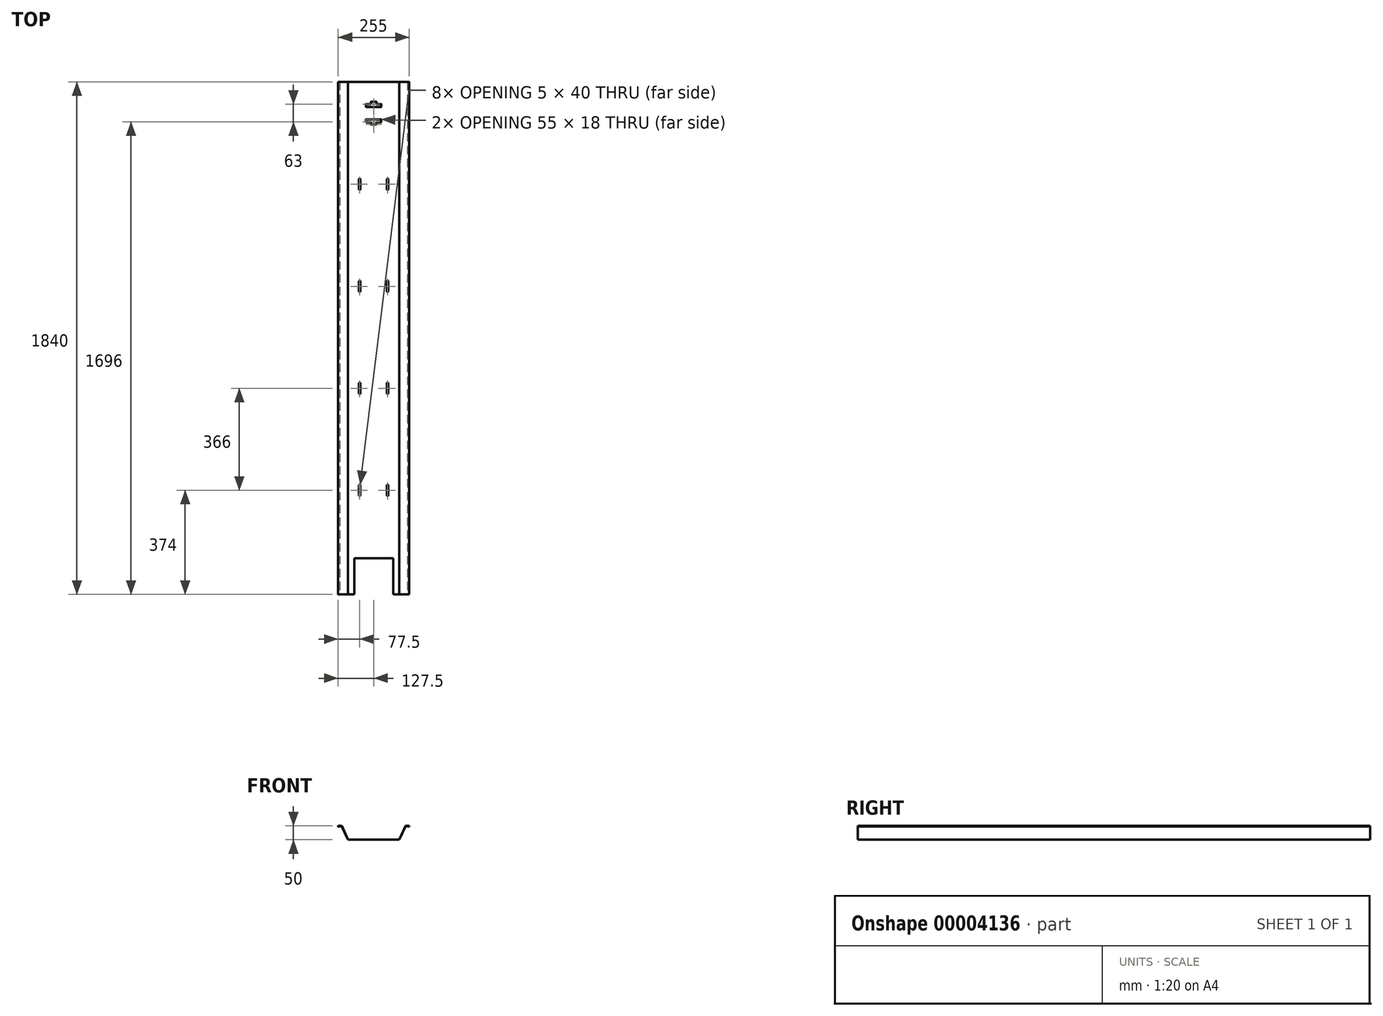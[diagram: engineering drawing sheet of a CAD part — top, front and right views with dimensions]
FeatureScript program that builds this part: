
annotation { "Feature Type Name" : "Feature", "Feature Type Description" : "" }
export const myFeature = defineFeature(function(context is Context, id is Id, definition is map)
    precondition{}
    {
        {
            var Q0;
            Q0=qCreatedBy(makeId("Front.planeOp"),FACE);
            var sketch = newSketch(context, id + "F0", { "sketchPlane" : qUnion([Q0])});
            skLineSegment(sketch, "E0", {"start": v(-92.5, 0) * mm, "end": v(0, 0) * mm});
            skLineSegment(sketch, "E1.0", {"start": v(-126.5, 48) * mm, "end": v(-121.5, 48) * mm});
            skLineSegment(sketch, "E1.1", {"start": v(-126.5, 49) * mm, "end": v(-126.5, 48) * mm});
            skLineSegment(sketch, "E1.2", {"start": v(-115.14, 49) * mm, "end": v(-126.5, 49) * mm});
            skLineSegment(sketch, "E2", {"start": v(-92.5, 0) * mm, "end": v(-115.14, 49) * mm});
            skLineSegment(sketch, "E3.0", {"start": v(-127.5, 47) * mm, "end": v(-121.5, 47) * mm});
            skLineSegment(sketch, "E3.1", {"start": v(-127.5, 50) * mm, "end": v(-127.5, 47) * mm});
            skLineSegment(sketch, "E3.2", {"start": v(-114.5, 50) * mm, "end": v(-127.5, 50) * mm});
            skLineSegment(sketch, "E3.3", {"start": v(-91.86, 1) * mm, "end": v(-114.5, 50) * mm});
            skLineSegment(sketch, "E3.4", {"start": v(-91.86, 1) * mm, "end": v(0, 1) * mm});
            skLineSegment(sketch, "E4", {"start": v(-121.5, 48) * mm, "end": v(-121.5, 47) * mm});
            skLineSegment(sketch, "E5.0.MirrorCS", {"start": v(91.86, 1) * mm, "end": v(0, 1) * mm});
            skLineSegment(sketch, "E5.1.MirrorCS", {"start": v(92.5, 0) * mm, "end": v(0, 0) * mm});
            skLineSegment(sketch, "E5.2.MirrorCS", {"start": v(92.5, 0) * mm, "end": v(115.14, 49) * mm});
            skLineSegment(sketch, "E5.3.MirrorCS", {"start": v(91.86, 1) * mm, "end": v(114.5, 50) * mm});
            skLineSegment(sketch, "E5.4.MirrorCS", {"start": v(114.5, 50) * mm, "end": v(127.5, 50) * mm});
            skLineSegment(sketch, "E5.5.MirrorCS", {"start": v(115.14, 49) * mm, "end": v(126.5, 49) * mm});
            skLineSegment(sketch, "E5.6.MirrorCS", {"start": v(126.5, 49) * mm, "end": v(126.5, 48) * mm});
            skLineSegment(sketch, "E5.7.MirrorCS", {"start": v(126.5, 48) * mm, "end": v(121.5, 48) * mm});
            skLineSegment(sketch, "E5.8.MirrorCS", {"start": v(121.5, 48) * mm, "end": v(121.5, 47) * mm});
            skLineSegment(sketch, "E5.9.MirrorCS", {"start": v(127.5, 50) * mm, "end": v(127.5, 47) * mm});
            skLineSegment(sketch, "E5.10.MirrorCS", {"start": v(127.5, 47) * mm, "end": v(121.5, 47) * mm});
            skSolve(sketch);
        }
        {
            var Q0;
            Q0=makeQuery(id+"F0.imprint","IMPRINT",FACE,{"disambiguationData":[TD([[makeQuery(id+"F0.imprint","IMPRINT",EDGE,{"derivedFrom":sQuery(id+"F0.wireOp",EDGE,"E0")}),1.0]])]});
            extrude(context, id + "F1", {"entities" : qUnion([Q0]), "oppositeDirection" : true, "depth" : 1840 * mm});
        }
        {
            var Q0;
            Q0=makeQuery(id+"F1.opExtrude","SWEPT_EDGE",EDGE,{"disambiguationData":[OSD([sQuery(id+"F0.wireOp",EDGE,"E3.0"),sQuery(id+"F0.wireOp",EDGE,"E3.1")])]});
            var Q1;
            Q1=makeQuery(id+"F1.opExtrude","SWEPT_EDGE",EDGE,{"disambiguationData":[OSD([sQuery(id+"F0.wireOp",EDGE,"E3.1"),sQuery(id+"F0.wireOp",EDGE,"E3.2")])]});
            var Q2;
            Q2=makeQuery(id+"F1.opExtrude","SWEPT_EDGE",EDGE,{"disambiguationData":[OSD([sQuery(id+"F0.wireOp",EDGE,"E3.2"),sQuery(id+"F0.wireOp",EDGE,"E3.3")])]});
            var Q3;
            Q3=makeQuery(id+"F1.opExtrude","SWEPT_EDGE",EDGE,{"disambiguationData":[OSD([sQuery(id+"F0.wireOp",EDGE,"E5.4.MirrorCS"),sQuery(id+"F0.wireOp",EDGE,"E5.9.MirrorCS")])]});
            var Q4;
            Q4=makeQuery(id+"F1.opExtrude","SWEPT_EDGE",EDGE,{"disambiguationData":[OSD([sQuery(id+"F0.wireOp",EDGE,"E5.9.MirrorCS"),sQuery(id+"F0.wireOp",EDGE,"E5.10.MirrorCS")])]});
            var Q5;
            Q5=makeQuery(id+"F1.opExtrude","SWEPT_EDGE",EDGE,{"disambiguationData":[OSD([sQuery(id+"F0.wireOp",EDGE,"E5.3.MirrorCS"),sQuery(id+"F0.wireOp",EDGE,"E5.4.MirrorCS")])]});
            fillet(context, id + "F2", {"entities" : qUnion([Q0, Q1, Q2, Q3, Q4, Q5]), "radius" : 0.2 * mm, "tangentPropagation" : true, "allowEdgeOverflow" : false});
        }
        {
            var Q0;
            Q0=makeQuery(id+"F1.opExtrude","SWEPT_EDGE",EDGE,{"disambiguationData":[OSD([sQuery(id+"F0.wireOp",EDGE,"E5.7.MirrorCS"),sQuery(id+"F0.wireOp",EDGE,"E5.8.MirrorCS")])]});
            var Q1;
            Q1=makeQuery(id+"F1.opExtrude","SWEPT_EDGE",EDGE,{"disambiguationData":[OSD([sQuery(id+"F0.wireOp",EDGE,"E5.8.MirrorCS"),sQuery(id+"F0.wireOp",EDGE,"E5.10.MirrorCS")])]});
            var Q2;
            Q2=makeQuery(id+"F1.opExtrude","SWEPT_EDGE",EDGE,{"disambiguationData":[OSD([sQuery(id+"F0.wireOp",EDGE,"E5.5.MirrorCS"),sQuery(id+"F0.wireOp",EDGE,"E5.6.MirrorCS")])]});
            var Q3;
            Q3=makeQuery(id+"F1.opExtrude","SWEPT_EDGE",EDGE,{"disambiguationData":[OSD([sQuery(id+"F0.wireOp",EDGE,"E5.2.MirrorCS"),sQuery(id+"F0.wireOp",EDGE,"E5.5.MirrorCS")])]});
            var Q4;
            Q4=makeQuery(id+"F1.opExtrude","SWEPT_EDGE",EDGE,{"disambiguationData":[OSD([sQuery(id+"F0.wireOp",EDGE,"E5.6.MirrorCS"),sQuery(id+"F0.wireOp",EDGE,"E5.7.MirrorCS")])]});
            var Q5;
            Q5=makeQuery(id+"F1.opExtrude","SWEPT_EDGE",EDGE,{"disambiguationData":[OSD([sQuery(id+"F0.wireOp",EDGE,"E1.0"),sQuery(id+"F0.wireOp",EDGE,"E1.1")])]});
            var Q6;
            Q6=makeQuery(id+"F1.opExtrude","SWEPT_EDGE",EDGE,{"disambiguationData":[OSD([sQuery(id+"F0.wireOp",EDGE,"E1.0"),sQuery(id+"F0.wireOp",EDGE,"E4")])]});
            var Q7;
            Q7=makeQuery(id+"F1.opExtrude","SWEPT_EDGE",EDGE,{"disambiguationData":[OSD([sQuery(id+"F0.wireOp",EDGE,"E3.0"),sQuery(id+"F0.wireOp",EDGE,"E4")])]});
            var Q8;
            Q8=makeQuery(id+"F1.opExtrude","SWEPT_EDGE",EDGE,{"disambiguationData":[OSD([sQuery(id+"F0.wireOp",EDGE,"E1.1"),sQuery(id+"F0.wireOp",EDGE,"E1.2")])]});
            var Q9;
            Q9=makeQuery(id+"F1.opExtrude","SWEPT_EDGE",EDGE,{"disambiguationData":[OSD([sQuery(id+"F0.wireOp",EDGE,"E1.2"),sQuery(id+"F0.wireOp",EDGE,"E2")])]});
            fillet(context, id + "F3", {"entities" : qUnion([Q0, Q1, Q2, Q3, Q4, Q5, Q6, Q7, Q8, Q9]), "radius" : 0.1 * mm, "tangentPropagation" : true, "allowEdgeOverflow" : false});
        }
        {
            var Q0;
            Q0=makeQuery(id+"F1.opExtrude","SWEPT_FACE",FACE,{"disambiguationData":[OSD([sQuery(id+"F0.wireOp",EDGE,"E5.0.MirrorCS")])]});
            var sketch = newSketch(context, id + "F4", { "sketchPlane" : qUnion([Q0])});
            skLineSegment(sketch, "E6", {"start": v(0, 0) * mm, "end": v(-70, 0) * mm});
            skLineSegment(sketch, "E7", {"start": v(-70, 0) * mm, "end": v(-70, 130) * mm});
            skLineSegment(sketch, "E8", {"start": v(-70, 130) * mm, "end": v(70, 130) * mm});
            skLineSegment(sketch, "E9", {"start": v(70, 130) * mm, "end": v(70, 0) * mm});
            skLineSegment(sketch, "E10", {"start": v(70, 0) * mm, "end": v(0, 0) * mm});
            skLineSegment(sketch, "E11", {"start": v(0, 1840) * mm, "end": v(0, 0) * mm, "construction": true});
            skLineSegment(sketch, "E12", {"start": v(0, 1750) * mm, "end": v(-27.5, 1750) * mm});
            skLineSegment(sketch, "E13", {"start": v(-27.5, 1750) * mm, "end": v(-27.5, 1760) * mm});
            skLineSegment(sketch, "E14", {"start": v(-27.5, 1760) * mm, "end": v(-10, 1760) * mm});
            skLineSegment(sketch, "E15", {"start": v(-10, 1760) * mm, "end": v(-10, 1768) * mm});
            skLineSegment(sketch, "E16", {"start": v(-10, 1768) * mm, "end": v(0, 1768) * mm});
            skLineSegment(sketch, "E17", {"start": v(0, 1768) * mm, "end": v(10, 1768) * mm});
            skLineSegment(sketch, "E18", {"start": v(10, 1768) * mm, "end": v(10, 1760) * mm});
            skLineSegment(sketch, "E19", {"start": v(10, 1760) * mm, "end": v(27.5, 1760) * mm});
            skLineSegment(sketch, "E20", {"start": v(27.5, 1760) * mm, "end": v(27.5, 1750) * mm});
            skLineSegment(sketch, "E21", {"start": v(27.5, 1750) * mm, "end": v(0, 1750) * mm});
            skLineSegment(sketch, "E22", {"start": v(0, 1705) * mm, "end": v(27.5, 1705) * mm});
            skLineSegment(sketch, "E23", {"start": v(27.5, 1705) * mm, "end": v(27.5, 1695) * mm});
            skLineSegment(sketch, "E24", {"start": v(27.5, 1695) * mm, "end": v(10, 1695) * mm});
            skLineSegment(sketch, "E25", {"start": v(10, 1695) * mm, "end": v(10, 1687) * mm});
            skLineSegment(sketch, "E26", {"start": v(10, 1687) * mm, "end": v(-10, 1687) * mm});
            skLineSegment(sketch, "E27", {"start": v(-10, 1687) * mm, "end": v(-10, 1695) * mm});
            skLineSegment(sketch, "E28", {"start": v(-10, 1695) * mm, "end": v(-27.5, 1695) * mm});
            skLineSegment(sketch, "E29", {"start": v(-27.5, 1695) * mm, "end": v(-27.5, 1705) * mm});
            skLineSegment(sketch, "E30", {"start": v(-27.5, 1705) * mm, "end": v(0, 1705) * mm});
            skLineSegment(sketch, "E31", {"start": v(-91.86, 1472) * mm, "end": v(91.86, 1472) * mm, "construction": true});
            skLineSegment(sketch, "E32", {"start": v(-91.86, 1106) * mm, "end": v(91.86, 1106) * mm, "construction": true});
            skLineSegment(sketch, "E33", {"start": v(-91.86, 740) * mm, "end": v(91.86, 740) * mm, "construction": true});
            skLineSegment(sketch, "E34", {"start": v(-91.86, 374) * mm, "end": v(91.86, 374) * mm, "construction": true});
            skLineSegment(sketch, "E35", {"start": v(50, 1840) * mm, "end": v(50, 0) * mm, "construction": true});
            skLineSegment(sketch, "E36", {"start": v(-50, 1840) * mm, "end": v(-50, 0) * mm, "construction": true});
            skLineSegment(sketch, "E37.rect.bottom", {"start": v(52.5, 354) * mm, "end": v(47.5, 354) * mm});
            skLineSegment(sketch, "E37.rect.top", {"start": v(52.5, 394) * mm, "end": v(47.5, 394) * mm});
            skLineSegment(sketch, "E37.rect.left", {"start": v(52.5, 354) * mm, "end": v(52.5, 394) * mm});
            skLineSegment(sketch, "E37.rect.right", {"start": v(47.5, 354) * mm, "end": v(47.5, 394) * mm});
            skPoint(sketch, "E37.rect.middle", {"position": v(50, 374) * mm});
            skLineSegment(sketch, "E38.rect.bottom", {"start": v(-47.5, 354) * mm, "end": v(-52.5, 354) * mm});
            skLineSegment(sketch, "E38.rect.top", {"start": v(-47.5, 394) * mm, "end": v(-52.5, 394) * mm});
            skLineSegment(sketch, "E38.rect.left", {"start": v(-47.5, 354) * mm, "end": v(-47.5, 394) * mm});
            skLineSegment(sketch, "E38.rect.right", {"start": v(-52.5, 354) * mm, "end": v(-52.5, 394) * mm});
            skPoint(sketch, "E38.rect.middle", {"position": v(-50, 374) * mm});
            skLineSegment(sketch, "E39.rect.bottom", {"start": v(-47.5, 720) * mm, "end": v(-52.5, 720) * mm});
            skLineSegment(sketch, "E39.rect.top", {"start": v(-47.5, 760) * mm, "end": v(-52.5, 760) * mm});
            skLineSegment(sketch, "E39.rect.left", {"start": v(-47.5, 720) * mm, "end": v(-47.5, 760) * mm});
            skLineSegment(sketch, "E39.rect.right", {"start": v(-52.5, 720) * mm, "end": v(-52.5, 760) * mm});
            skPoint(sketch, "E39.rect.middle", {"position": v(-50, 740) * mm});
            skLineSegment(sketch, "E40.rect.bottom", {"start": v(52.5, 720) * mm, "end": v(47.5, 720) * mm});
            skLineSegment(sketch, "E40.rect.top", {"start": v(52.5, 760) * mm, "end": v(47.5, 760) * mm});
            skLineSegment(sketch, "E40.rect.left", {"start": v(52.5, 720) * mm, "end": v(52.5, 760) * mm});
            skLineSegment(sketch, "E40.rect.right", {"start": v(47.5, 720) * mm, "end": v(47.5, 760) * mm});
            skPoint(sketch, "E40.rect.middle", {"position": v(50, 740) * mm});
            skLineSegment(sketch, "E41.rect.bottom", {"start": v(-47.5, 1086) * mm, "end": v(-52.5, 1086) * mm});
            skLineSegment(sketch, "E41.rect.top", {"start": v(-47.5, 1126) * mm, "end": v(-52.5, 1126) * mm});
            skLineSegment(sketch, "E41.rect.left", {"start": v(-47.5, 1086) * mm, "end": v(-47.5, 1126) * mm});
            skLineSegment(sketch, "E41.rect.right", {"start": v(-52.5, 1086) * mm, "end": v(-52.5, 1126) * mm});
            skPoint(sketch, "E41.rect.middle", {"position": v(-50, 1106) * mm});
            skLineSegment(sketch, "E42.rect.bottom", {"start": v(52.5, 1086) * mm, "end": v(47.5, 1086) * mm});
            skLineSegment(sketch, "E42.rect.top", {"start": v(52.5, 1126) * mm, "end": v(47.5, 1126) * mm});
            skLineSegment(sketch, "E42.rect.left", {"start": v(52.5, 1086) * mm, "end": v(52.5, 1126) * mm});
            skLineSegment(sketch, "E42.rect.right", {"start": v(47.5, 1086) * mm, "end": v(47.5, 1126) * mm});
            skPoint(sketch, "E42.rect.middle", {"position": v(50, 1106) * mm});
            skLineSegment(sketch, "E43.rect.bottom", {"start": v(-47.5, 1452) * mm, "end": v(-52.5, 1452) * mm});
            skLineSegment(sketch, "E43.rect.top", {"start": v(-47.5, 1492) * mm, "end": v(-52.5, 1492) * mm});
            skLineSegment(sketch, "E43.rect.left", {"start": v(-47.5, 1452) * mm, "end": v(-47.5, 1492) * mm});
            skLineSegment(sketch, "E43.rect.right", {"start": v(-52.5, 1452) * mm, "end": v(-52.5, 1492) * mm});
            skPoint(sketch, "E43.rect.middle", {"position": v(-50, 1472) * mm});
            skLineSegment(sketch, "E44.rect.bottom", {"start": v(52.5, 1452) * mm, "end": v(47.5, 1452) * mm});
            skLineSegment(sketch, "E44.rect.top", {"start": v(52.5, 1492) * mm, "end": v(47.5, 1492) * mm});
            skLineSegment(sketch, "E44.rect.left", {"start": v(52.5, 1452) * mm, "end": v(52.5, 1492) * mm});
            skLineSegment(sketch, "E44.rect.right", {"start": v(47.5, 1452) * mm, "end": v(47.5, 1492) * mm});
            skPoint(sketch, "E44.rect.middle", {"position": v(50, 1472) * mm});
            skSolve(sketch);
        }
        {
            var Q0;
            Q0=makeQuery(id+"F4.imprint","IMPRINT",FACE,{"disambiguationData":[TD([[makeQuery(id+"F4.imprint","IMPRINT",EDGE,{"derivedFrom":sQuery(id+"F4.wireOp",EDGE,"E6")}),-1.0]])]});
            var Q1;
            Q1=makeQuery(id+"F4.imprint","IMPRINT",FACE,{"disambiguationData":[TD([[makeQuery(id+"F4.imprint","IMPRINT",EDGE,{"derivedFrom":sQuery(id+"F4.wireOp",EDGE,"E37.rect.bottom")}),-1.0]])]});
            var Q2;
            Q2=makeQuery(id+"F4.imprint","IMPRINT",FACE,{"disambiguationData":[TD([[makeQuery(id+"F4.imprint","IMPRINT",EDGE,{"derivedFrom":sQuery(id+"F4.wireOp",EDGE,"E38.rect.bottom")}),-1.0]])]});
            var Q3;
            Q3=makeQuery(id+"F4.imprint","IMPRINT",FACE,{"disambiguationData":[TD([[makeQuery(id+"F4.imprint","IMPRINT",EDGE,{"derivedFrom":sQuery(id+"F4.wireOp",EDGE,"E39.rect.bottom")}),-1.0]])]});
            var Q4;
            Q4=makeQuery(id+"F4.imprint","IMPRINT",FACE,{"disambiguationData":[TD([[makeQuery(id+"F4.imprint","IMPRINT",EDGE,{"derivedFrom":sQuery(id+"F4.wireOp",EDGE,"E40.rect.bottom")}),-1.0]])]});
            var Q5;
            Q5=makeQuery(id+"F4.imprint","IMPRINT",FACE,{"disambiguationData":[TD([[makeQuery(id+"F4.imprint","IMPRINT",EDGE,{"derivedFrom":sQuery(id+"F4.wireOp",EDGE,"E42.rect.bottom")}),-1.0]])]});
            var Q6;
            Q6=makeQuery(id+"F4.imprint","IMPRINT",FACE,{"disambiguationData":[TD([[makeQuery(id+"F4.imprint","IMPRINT",EDGE,{"derivedFrom":sQuery(id+"F4.wireOp",EDGE,"E41.rect.bottom")}),-1.0]])]});
            var Q7;
            Q7=makeQuery(id+"F4.imprint","IMPRINT",FACE,{"disambiguationData":[TD([[makeQuery(id+"F4.imprint","IMPRINT",EDGE,{"derivedFrom":sQuery(id+"F4.wireOp",EDGE,"E44.rect.bottom")}),-1.0]])]});
            var Q8;
            Q8=makeQuery(id+"F4.imprint","IMPRINT",FACE,{"disambiguationData":[TD([[makeQuery(id+"F4.imprint","IMPRINT",EDGE,{"derivedFrom":sQuery(id+"F4.wireOp",EDGE,"E43.rect.bottom")}),-1.0]])]});
            var Q9;
            Q9=makeQuery(id+"F4.imprint","IMPRINT",FACE,{"disambiguationData":[TD([[makeQuery(id+"F4.imprint","IMPRINT",EDGE,{"derivedFrom":sQuery(id+"F4.wireOp",EDGE,"E22")}),-1.0]])]});
            var Q10;
            Q10=makeQuery(id+"F4.imprint","IMPRINT",FACE,{"disambiguationData":[TD([[makeQuery(id+"F4.imprint","IMPRINT",EDGE,{"derivedFrom":sQuery(id+"F4.wireOp",EDGE,"E12")}),-1.0]])]});
            extrude(context, id + "F5", {"entities" : qUnion([Q0, Q1, Q2, Q3, Q4, Q5, Q6, Q7, Q8, Q9, Q10]), "operationType" : NewBodyOperationType.REMOVE, "oppositeDirection" : true, "depth" : 25 * mm});
        }
        {
            var Q0;
            Q0=makeQuery(id+"F5.boolean.opBoolean","COPY",EDGE,{"derivedFrom":makeQuery(id+"F5.opExtrude","SWEPT_EDGE",EDGE,{"disambiguationData":[OSD([sQuery(id+"F4.wireOp",EDGE,"E38.rect.top"),sQuery(id+"F4.wireOp",EDGE,"E38.rect.right")])]})});
            var Q1;
            Q1=makeQuery(id+"F5.boolean.opBoolean","COPY",EDGE,{"derivedFrom":makeQuery(id+"F5.opExtrude","SWEPT_EDGE",EDGE,{"disambiguationData":[OSD([sQuery(id+"F4.wireOp",EDGE,"E38.rect.top"),sQuery(id+"F4.wireOp",EDGE,"E38.rect.left")])]})});
            var Q2;
            Q2=makeQuery(id+"F5.boolean.opBoolean","COPY",EDGE,{"derivedFrom":makeQuery(id+"F5.opExtrude","SWEPT_EDGE",EDGE,{"disambiguationData":[OSD([sQuery(id+"F4.wireOp",EDGE,"E38.rect.bottom"),sQuery(id+"F4.wireOp",EDGE,"E38.rect.right")])]})});
            var Q3;
            Q3=makeQuery(id+"F5.boolean.opBoolean","COPY",EDGE,{"derivedFrom":makeQuery(id+"F5.opExtrude","SWEPT_EDGE",EDGE,{"disambiguationData":[OSD([sQuery(id+"F4.wireOp",EDGE,"E38.rect.bottom"),sQuery(id+"F4.wireOp",EDGE,"E38.rect.left")])]})});
            var Q4;
            Q4=makeQuery(id+"F5.boolean.opBoolean","COPY",EDGE,{"derivedFrom":makeQuery(id+"F5.opExtrude","SWEPT_EDGE",EDGE,{"disambiguationData":[OSD([sQuery(id+"F4.wireOp",EDGE,"E37.rect.bottom"),sQuery(id+"F4.wireOp",EDGE,"E37.rect.right")])]})});
            var Q5;
            Q5=makeQuery(id+"F5.boolean.opBoolean","COPY",EDGE,{"derivedFrom":makeQuery(id+"F5.opExtrude","SWEPT_EDGE",EDGE,{"disambiguationData":[OSD([sQuery(id+"F4.wireOp",EDGE,"E37.rect.bottom"),sQuery(id+"F4.wireOp",EDGE,"E37.rect.left")])]})});
            var Q6;
            Q6=makeQuery(id+"F5.boolean.opBoolean","COPY",EDGE,{"derivedFrom":makeQuery(id+"F5.opExtrude","SWEPT_EDGE",EDGE,{"disambiguationData":[OSD([sQuery(id+"F4.wireOp",EDGE,"E37.rect.top"),sQuery(id+"F4.wireOp",EDGE,"E37.rect.left")])]})});
            var Q7;
            Q7=makeQuery(id+"F5.boolean.opBoolean","COPY",EDGE,{"derivedFrom":makeQuery(id+"F5.opExtrude","SWEPT_EDGE",EDGE,{"disambiguationData":[OSD([sQuery(id+"F4.wireOp",EDGE,"E37.rect.top"),sQuery(id+"F4.wireOp",EDGE,"E37.rect.right")])]})});
            var Q8;
            Q8=makeQuery(id+"F5.boolean.opBoolean","COPY",EDGE,{"derivedFrom":makeQuery(id+"F5.opExtrude","SWEPT_EDGE",EDGE,{"disambiguationData":[OSD([sQuery(id+"F4.wireOp",EDGE,"E39.rect.top"),sQuery(id+"F4.wireOp",EDGE,"E39.rect.right")])]})});
            var Q9;
            Q9=makeQuery(id+"F5.boolean.opBoolean","COPY",EDGE,{"derivedFrom":makeQuery(id+"F5.opExtrude","SWEPT_EDGE",EDGE,{"disambiguationData":[OSD([sQuery(id+"F4.wireOp",EDGE,"E39.rect.top"),sQuery(id+"F4.wireOp",EDGE,"E39.rect.left")])]})});
            var Q10;
            Q10=makeQuery(id+"F5.boolean.opBoolean","COPY",EDGE,{"derivedFrom":makeQuery(id+"F5.opExtrude","SWEPT_EDGE",EDGE,{"disambiguationData":[OSD([sQuery(id+"F4.wireOp",EDGE,"E39.rect.bottom"),sQuery(id+"F4.wireOp",EDGE,"E39.rect.right")])]})});
            var Q11;
            Q11=makeQuery(id+"F5.boolean.opBoolean","COPY",EDGE,{"derivedFrom":makeQuery(id+"F5.opExtrude","SWEPT_EDGE",EDGE,{"disambiguationData":[OSD([sQuery(id+"F4.wireOp",EDGE,"E39.rect.bottom"),sQuery(id+"F4.wireOp",EDGE,"E39.rect.left")])]})});
            var Q12;
            Q12=makeQuery(id+"F5.boolean.opBoolean","COPY",EDGE,{"derivedFrom":makeQuery(id+"F5.opExtrude","SWEPT_EDGE",EDGE,{"disambiguationData":[OSD([sQuery(id+"F4.wireOp",EDGE,"E40.rect.bottom"),sQuery(id+"F4.wireOp",EDGE,"E40.rect.left")])]})});
            var Q13;
            Q13=makeQuery(id+"F5.boolean.opBoolean","COPY",EDGE,{"derivedFrom":makeQuery(id+"F5.opExtrude","SWEPT_EDGE",EDGE,{"disambiguationData":[OSD([sQuery(id+"F4.wireOp",EDGE,"E40.rect.bottom"),sQuery(id+"F4.wireOp",EDGE,"E40.rect.right")])]})});
            var Q14;
            Q14=makeQuery(id+"F5.boolean.opBoolean","COPY",EDGE,{"derivedFrom":makeQuery(id+"F5.opExtrude","SWEPT_EDGE",EDGE,{"disambiguationData":[OSD([sQuery(id+"F4.wireOp",EDGE,"E40.rect.top"),sQuery(id+"F4.wireOp",EDGE,"E40.rect.right")])]})});
            var Q15;
            Q15=makeQuery(id+"F5.boolean.opBoolean","COPY",EDGE,{"derivedFrom":makeQuery(id+"F5.opExtrude","SWEPT_EDGE",EDGE,{"disambiguationData":[OSD([sQuery(id+"F4.wireOp",EDGE,"E40.rect.top"),sQuery(id+"F4.wireOp",EDGE,"E40.rect.left")])]})});
            var Q16;
            Q16=makeQuery(id+"F5.boolean.opBoolean","COPY",EDGE,{"derivedFrom":makeQuery(id+"F5.opExtrude","SWEPT_EDGE",EDGE,{"disambiguationData":[OSD([sQuery(id+"F4.wireOp",EDGE,"E42.rect.top"),sQuery(id+"F4.wireOp",EDGE,"E42.rect.left")])]})});
            var Q17;
            Q17=makeQuery(id+"F5.boolean.opBoolean","COPY",EDGE,{"derivedFrom":makeQuery(id+"F5.opExtrude","SWEPT_EDGE",EDGE,{"disambiguationData":[OSD([sQuery(id+"F4.wireOp",EDGE,"E42.rect.top"),sQuery(id+"F4.wireOp",EDGE,"E42.rect.right")])]})});
            var Q18;
            Q18=makeQuery(id+"F5.boolean.opBoolean","COPY",EDGE,{"derivedFrom":makeQuery(id+"F5.opExtrude","SWEPT_EDGE",EDGE,{"disambiguationData":[OSD([sQuery(id+"F4.wireOp",EDGE,"E42.rect.bottom"),sQuery(id+"F4.wireOp",EDGE,"E42.rect.left")])]})});
            var Q19;
            Q19=makeQuery(id+"F5.boolean.opBoolean","COPY",EDGE,{"derivedFrom":makeQuery(id+"F5.opExtrude","SWEPT_EDGE",EDGE,{"disambiguationData":[OSD([sQuery(id+"F4.wireOp",EDGE,"E42.rect.bottom"),sQuery(id+"F4.wireOp",EDGE,"E42.rect.right")])]})});
            var Q20;
            Q20=makeQuery(id+"F5.boolean.opBoolean","COPY",EDGE,{"derivedFrom":makeQuery(id+"F5.opExtrude","SWEPT_EDGE",EDGE,{"disambiguationData":[OSD([sQuery(id+"F4.wireOp",EDGE,"E41.rect.bottom"),sQuery(id+"F4.wireOp",EDGE,"E41.rect.right")])]})});
            var Q21;
            Q21=makeQuery(id+"F5.boolean.opBoolean","COPY",EDGE,{"derivedFrom":makeQuery(id+"F5.opExtrude","SWEPT_EDGE",EDGE,{"disambiguationData":[OSD([sQuery(id+"F4.wireOp",EDGE,"E41.rect.bottom"),sQuery(id+"F4.wireOp",EDGE,"E41.rect.left")])]})});
            var Q22;
            Q22=makeQuery(id+"F5.boolean.opBoolean","COPY",EDGE,{"derivedFrom":makeQuery(id+"F5.opExtrude","SWEPT_EDGE",EDGE,{"disambiguationData":[OSD([sQuery(id+"F4.wireOp",EDGE,"E41.rect.top"),sQuery(id+"F4.wireOp",EDGE,"E41.rect.left")])]})});
            var Q23;
            Q23=makeQuery(id+"F5.boolean.opBoolean","COPY",EDGE,{"derivedFrom":makeQuery(id+"F5.opExtrude","SWEPT_EDGE",EDGE,{"disambiguationData":[OSD([sQuery(id+"F4.wireOp",EDGE,"E41.rect.top"),sQuery(id+"F4.wireOp",EDGE,"E41.rect.right")])]})});
            var Q24;
            Q24=makeQuery(id+"F5.boolean.opBoolean","COPY",EDGE,{"derivedFrom":makeQuery(id+"F5.opExtrude","SWEPT_EDGE",EDGE,{"disambiguationData":[OSD([sQuery(id+"F4.wireOp",EDGE,"E43.rect.top"),sQuery(id+"F4.wireOp",EDGE,"E43.rect.right")])]})});
            var Q25;
            Q25=makeQuery(id+"F5.boolean.opBoolean","COPY",EDGE,{"derivedFrom":makeQuery(id+"F5.opExtrude","SWEPT_EDGE",EDGE,{"disambiguationData":[OSD([sQuery(id+"F4.wireOp",EDGE,"E43.rect.top"),sQuery(id+"F4.wireOp",EDGE,"E43.rect.left")])]})});
            var Q26;
            Q26=makeQuery(id+"F5.boolean.opBoolean","COPY",EDGE,{"derivedFrom":makeQuery(id+"F5.opExtrude","SWEPT_EDGE",EDGE,{"disambiguationData":[OSD([sQuery(id+"F4.wireOp",EDGE,"E43.rect.bottom"),sQuery(id+"F4.wireOp",EDGE,"E43.rect.left")])]})});
            var Q27;
            Q27=makeQuery(id+"F5.boolean.opBoolean","COPY",EDGE,{"derivedFrom":makeQuery(id+"F5.opExtrude","SWEPT_EDGE",EDGE,{"disambiguationData":[OSD([sQuery(id+"F4.wireOp",EDGE,"E43.rect.bottom"),sQuery(id+"F4.wireOp",EDGE,"E43.rect.right")])]})});
            var Q28;
            Q28=makeQuery(id+"F5.boolean.opBoolean","COPY",EDGE,{"derivedFrom":makeQuery(id+"F5.opExtrude","SWEPT_EDGE",EDGE,{"disambiguationData":[OSD([sQuery(id+"F4.wireOp",EDGE,"E44.rect.bottom"),sQuery(id+"F4.wireOp",EDGE,"E44.rect.right")])]})});
            var Q29;
            Q29=makeQuery(id+"F5.boolean.opBoolean","COPY",EDGE,{"derivedFrom":makeQuery(id+"F5.opExtrude","SWEPT_EDGE",EDGE,{"disambiguationData":[OSD([sQuery(id+"F4.wireOp",EDGE,"E44.rect.bottom"),sQuery(id+"F4.wireOp",EDGE,"E44.rect.left")])]})});
            var Q30;
            Q30=makeQuery(id+"F5.boolean.opBoolean","COPY",EDGE,{"derivedFrom":makeQuery(id+"F5.opExtrude","SWEPT_EDGE",EDGE,{"disambiguationData":[OSD([sQuery(id+"F4.wireOp",EDGE,"E44.rect.top"),sQuery(id+"F4.wireOp",EDGE,"E44.rect.left")])]})});
            var Q31;
            Q31=makeQuery(id+"F5.boolean.opBoolean","COPY",EDGE,{"derivedFrom":makeQuery(id+"F5.opExtrude","SWEPT_EDGE",EDGE,{"disambiguationData":[OSD([sQuery(id+"F4.wireOp",EDGE,"E44.rect.top"),sQuery(id+"F4.wireOp",EDGE,"E44.rect.right")])]})});
            fillet(context, id + "F6", {"entities" : qUnion([Q0, Q1, Q2, Q3, Q4, Q5, Q6, Q7, Q8, Q9, Q10, Q11, Q12, Q13, Q14, Q15, Q16, Q17, Q18, Q19, Q20, Q21, Q22, Q23, Q24, Q25, Q26, Q27, Q28, Q29, Q30, Q31]), "radius" : 2 * mm, "tangentPropagation" : true, "allowEdgeOverflow" : false});
        }
        {
            var Q0;
            Q0=makeQuery(id+"F5.boolean.opBoolean","COPY",EDGE,{"derivedFrom":makeQuery(id+"F5.opExtrude","SWEPT_EDGE",EDGE,{"disambiguationData":[OSD([sQuery(id+"F4.wireOp",EDGE,"E18"),sQuery(id+"F4.wireOp",EDGE,"E19")])]})});
            var Q1;
            Q1=makeQuery(id+"F5.boolean.opBoolean","COPY",EDGE,{"derivedFrom":makeQuery(id+"F5.opExtrude","SWEPT_EDGE",EDGE,{"disambiguationData":[OSD([sQuery(id+"F4.wireOp",EDGE,"E17"),sQuery(id+"F4.wireOp",EDGE,"E18")])]})});
            var Q2;
            Q2=makeQuery(id+"F5.boolean.opBoolean","COPY",EDGE,{"derivedFrom":makeQuery(id+"F5.opExtrude","SWEPT_EDGE",EDGE,{"disambiguationData":[OSD([sQuery(id+"F4.wireOp",EDGE,"E19"),sQuery(id+"F4.wireOp",EDGE,"E20")])]})});
            var Q3;
            Q3=makeQuery(id+"F5.boolean.opBoolean","COPY",EDGE,{"derivedFrom":makeQuery(id+"F5.opExtrude","SWEPT_EDGE",EDGE,{"disambiguationData":[OSD([sQuery(id+"F4.wireOp",EDGE,"E20"),sQuery(id+"F4.wireOp",EDGE,"E21")])]})});
            var Q4;
            Q4=makeQuery(id+"F5.boolean.opBoolean","COPY",EDGE,{"derivedFrom":makeQuery(id+"F5.opExtrude","SWEPT_EDGE",EDGE,{"disambiguationData":[OSD([sQuery(id+"F4.wireOp",EDGE,"E15"),sQuery(id+"F4.wireOp",EDGE,"E16")])]})});
            var Q5;
            Q5=makeQuery(id+"F5.boolean.opBoolean","COPY",EDGE,{"derivedFrom":makeQuery(id+"F5.opExtrude","SWEPT_EDGE",EDGE,{"disambiguationData":[OSD([sQuery(id+"F4.wireOp",EDGE,"E14"),sQuery(id+"F4.wireOp",EDGE,"E15")])]})});
            var Q6;
            Q6=makeQuery(id+"F5.boolean.opBoolean","COPY",EDGE,{"derivedFrom":makeQuery(id+"F5.opExtrude","SWEPT_EDGE",EDGE,{"disambiguationData":[OSD([sQuery(id+"F4.wireOp",EDGE,"E13"),sQuery(id+"F4.wireOp",EDGE,"E14")])]})});
            var Q7;
            Q7=makeQuery(id+"F5.boolean.opBoolean","COPY",EDGE,{"derivedFrom":makeQuery(id+"F5.opExtrude","SWEPT_EDGE",EDGE,{"disambiguationData":[OSD([sQuery(id+"F4.wireOp",EDGE,"E12"),sQuery(id+"F4.wireOp",EDGE,"E13")])]})});
            var Q8;
            Q8=makeQuery(id+"F5.boolean.opBoolean","COPY",EDGE,{"derivedFrom":makeQuery(id+"F5.opExtrude","SWEPT_EDGE",EDGE,{"disambiguationData":[OSD([sQuery(id+"F4.wireOp",EDGE,"E29"),sQuery(id+"F4.wireOp",EDGE,"E30")])]})});
            var Q9;
            Q9=makeQuery(id+"F5.boolean.opBoolean","COPY",EDGE,{"derivedFrom":makeQuery(id+"F5.opExtrude","SWEPT_EDGE",EDGE,{"disambiguationData":[OSD([sQuery(id+"F4.wireOp",EDGE,"E28"),sQuery(id+"F4.wireOp",EDGE,"E29")])]})});
            var Q10;
            Q10=makeQuery(id+"F5.boolean.opBoolean","COPY",EDGE,{"derivedFrom":makeQuery(id+"F5.opExtrude","SWEPT_EDGE",EDGE,{"disambiguationData":[OSD([sQuery(id+"F4.wireOp",EDGE,"E27"),sQuery(id+"F4.wireOp",EDGE,"E28")])]})});
            var Q11;
            Q11=makeQuery(id+"F5.boolean.opBoolean","COPY",EDGE,{"derivedFrom":makeQuery(id+"F5.opExtrude","SWEPT_EDGE",EDGE,{"disambiguationData":[OSD([sQuery(id+"F4.wireOp",EDGE,"E26"),sQuery(id+"F4.wireOp",EDGE,"E27")])]})});
            var Q12;
            Q12=makeQuery(id+"F5.boolean.opBoolean","COPY",EDGE,{"derivedFrom":makeQuery(id+"F5.opExtrude","SWEPT_EDGE",EDGE,{"disambiguationData":[OSD([sQuery(id+"F4.wireOp",EDGE,"E25"),sQuery(id+"F4.wireOp",EDGE,"E26")])]})});
            var Q13;
            Q13=makeQuery(id+"F5.boolean.opBoolean","COPY",EDGE,{"derivedFrom":makeQuery(id+"F5.opExtrude","SWEPT_EDGE",EDGE,{"disambiguationData":[OSD([sQuery(id+"F4.wireOp",EDGE,"E24"),sQuery(id+"F4.wireOp",EDGE,"E25")])]})});
            var Q14;
            Q14=makeQuery(id+"F5.boolean.opBoolean","COPY",EDGE,{"derivedFrom":makeQuery(id+"F5.opExtrude","SWEPT_EDGE",EDGE,{"disambiguationData":[OSD([sQuery(id+"F4.wireOp",EDGE,"E23"),sQuery(id+"F4.wireOp",EDGE,"E24")])]})});
            var Q15;
            Q15=makeQuery(id+"F5.boolean.opBoolean","COPY",EDGE,{"derivedFrom":makeQuery(id+"F5.opExtrude","SWEPT_EDGE",EDGE,{"disambiguationData":[OSD([sQuery(id+"F4.wireOp",EDGE,"E22"),sQuery(id+"F4.wireOp",EDGE,"E23")])]})});
            fillet(context, id + "F7", {"entities" : qUnion([Q0, Q1, Q2, Q3, Q4, Q5, Q6, Q7, Q8, Q9, Q10, Q11, Q12, Q13, Q14, Q15]), "radius" : 0.1 * mm, "tangentPropagation" : true, "allowEdgeOverflow" : false});
        }
    });
